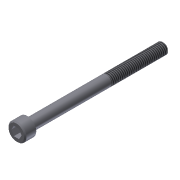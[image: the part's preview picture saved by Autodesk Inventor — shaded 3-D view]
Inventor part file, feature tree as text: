
AUTODESK INVENTOR PART (.ipt)
format: ipt  version: 2013 (Build 170138000, 138)  size: 96,256 bytes
history: native  units: in
note: dims shown in document units (in); Inventor stores cm internally (conversion verified against a paired STEP export)
features: extrude x3, sketch x3, chamfer x2, thread x1
ambient origin geometry x8: Origin, YZ Plane, XZ Plane, XY Plane, X Axis, Y Axis, Z Axis, Center Point
bodies: Solid1 (feature_tree)
feature tree (9):
  extrude  "Extrusion1"  Depth=0.19in TaperAngle=0.0deg
  extrude  "Extrusion2"  Depth=2.375in TaperAngle=0.0deg
  extrude  "Extrusion3"  Depth=0.125in TaperAngle=0.0deg
  thread  "Thread1"  [1 undecoded]
  chamfer  "Chamfer1"  Distance=0.02in Angle=45.0deg
  chamfer  "Chamfer2"  Distance=0.02in Angle=45.0deg
  sketch  "Sketch1"  dims[d0=0.312in d1=0.19in d2=0.0in]
  sketch  "Sketch2"  dims[d3=0.19in d4=2.375in d5=0.0in]
  sketch  "Sketch3"  dims[d6=0.1562in d7=0.125in d8=0.0in d9=1.0in d10=0.0in d11=0.02in d12=0.125in d13=45.0deg d14=0.02in d15=0.125in d16=45.0deg]
note: 1 required parameter value undecoded (feature->parameter linkage not recoverable at this tier; creation-order binding heuristic only, values carry confidence <= 0.55)
